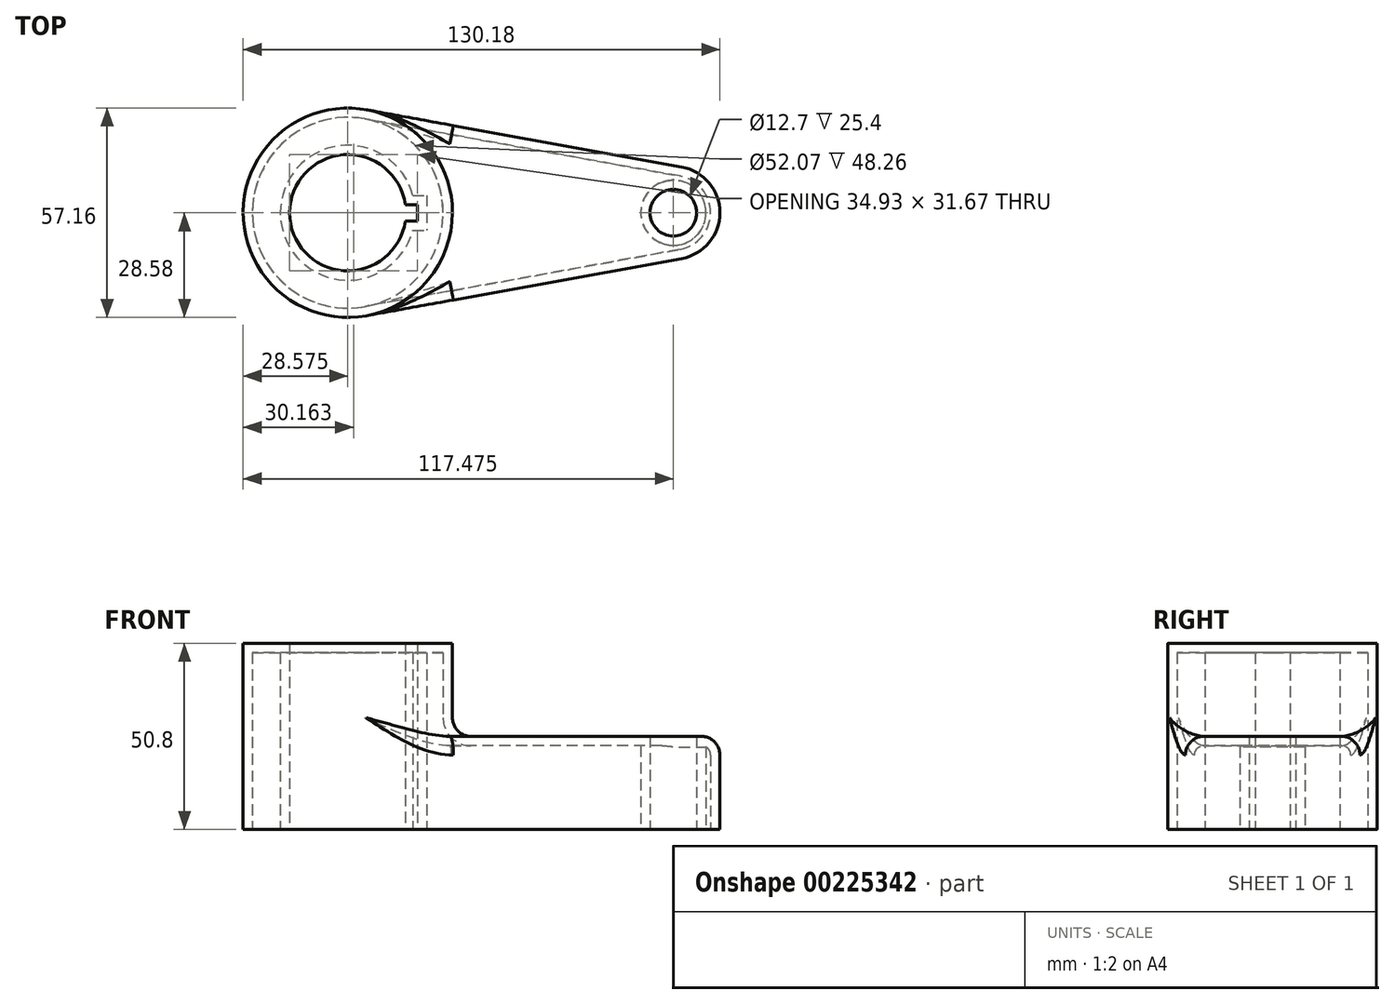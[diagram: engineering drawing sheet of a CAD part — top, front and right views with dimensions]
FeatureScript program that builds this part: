
annotation { "Feature Type Name" : "Feature", "Feature Type Description" : "" }
export const myFeature = defineFeature(function(context is Context, id is Id, definition is map)
    precondition{}
    {
        {
            var Q0;
            Q0=qCreatedBy(makeId("Top.planeOp"),FACE);
            var sketch = newSketch(context, id + "F0", { "sketchPlane" : qUnion([Q0])});
            skCircle(sketch, "E0", {"center": v(-65.9, 0) * mm, "radius": 28.58 * mm});
            skCircle(sketch, "E1", {"center": v(23, 0) * mm, "radius": 12.7 * mm});
            skLineSegment(sketch, "E2", {"start": v(-60.8, 28.12) * mm, "end": v(25.27, 12.5) * mm});
            skLineSegment(sketch, "E3", {"start": v(25.27, -12.5) * mm, "end": v(-60.8, -28.12) * mm});
            skCircle(sketch, "E4", {"center": v(-65.9, 0) * mm, "radius": 15.88 * mm});
            skCircle(sketch, "E5", {"center": v(23, 0) * mm, "radius": 6.35 * mm});
            skLineSegment(sketch, "E6.bottom", {"start": v(-50.18, 2.22) * mm, "end": v(-46.84, 2.22) * mm});
            skLineSegment(sketch, "E6.top", {"start": v(-50.18, -2.22) * mm, "end": v(-46.84, -2.22) * mm});
            skLineSegment(sketch, "E6.left", {"start": v(-50.18, 2.22) * mm, "end": v(-50.18, -2.22) * mm});
            skLineSegment(sketch, "E6.right", {"start": v(-46.84, 2.22) * mm, "end": v(-46.84, -2.22) * mm});
            skLineSegment(sketch, "E7", {"start": v(-65.9, 0) * mm, "end": v(-50.18, 2.22) * mm, "construction": true});
            skLineSegment(sketch, "E8", {"start": v(-65.9, 0) * mm, "end": v(-50.18, -2.22) * mm, "construction": true});
            skLineSegment(sketch, "E9", {"start": v(-65.9, 0) * mm, "end": v(-46.84, 0) * mm, "construction": true});
            skLineSegment(sketch, "E10", {"start": v(-81.77, 0) * mm, "end": v(-94.47, 0) * mm, "construction": true});
            skLineSegment(sketch, "E11", {"start": v(29.36, 0) * mm, "end": v(10.3, 0) * mm, "construction": true});
            skLineSegment(sketch, "E12", {"start": v(-65.9, 0) * mm, "end": v(23, 0) * mm, "construction": true});
            skSolve(sketch);
        }
        {
            var Q0;
            {var subQ0=sQuery(id+"F0.wireOp",EDGE,"E6.bottom");Q0=makeQuery(id+"F0.imprint","IMPRINT",FACE,{"disambiguationData":[TD([[makeQuery(id+"F0.imprint","IMPRINT",EDGE,{"derivedFrom":subQ0}),1.0]])]});}
            extrude(context, id + "F1", {"entities" : qUnion([Q0]), "depth" : 50.8 * mm});
        }
        {
            var Q0;
            Q0 = qSketchRegion(id + "F0", true);
            extrude(context, id + "F2", {"entities" : qUnion([Q0]), "operationType" : NewBodyOperationType.ADD, "depth" : 25.4 * mm});
        }
        {
            var Q0;
            {var subQ0=sQuery(id+"F0.wireOp",EDGE,"E0");Q0=makeQuery(id+"F2.boolean.opBoolean","INTERSECT",EDGE,{"derivedFrom":[makeQuery(id+"F1.opExtrude","SWEPT_FACE",FACE,{"disambiguationData":[OSD([subQ0])]}),makeQuery(id+"F2.opExtrude","CAP_FACE",FACE,{"disambiguationData":[OSD([subQ0,sQuery(id+"F0.wireOp",EDGE,"E1"),sQuery(id+"F0.wireOp",EDGE,"E2"),sQuery(id+"F0.wireOp",EDGE,"E3"),sQuery(id+"F0.wireOp",EDGE,"E4"),sQuery(id+"F0.wireOp",EDGE,"E5"),sQuery(id+"F0.wireOp",EDGE,"E6.bottom"),sQuery(id+"F0.wireOp",EDGE,"E6.top"),sQuery(id+"F0.wireOp",EDGE,"E6.right")])],"isStart":false})]});}
            fillet(context, id + "F3", {"entities" : qUnion([Q0]), "radius" : 5.08 * mm, "tangentPropagation" : true, "allowEdgeOverflow" : false});
        }
        {
            var Q0;
            Q0=makeQuery(id+"F2.opExtrude","CAP_EDGE",EDGE,{"disambiguationData":[OSD([sQuery(id+"F0.wireOp",EDGE,"E3")])],"isStart":false});
            fillet(context, id + "F4", {"entities" : qUnion([Q0]), "radius" : 5.08 * mm, "tangentPropagation" : true, "allowEdgeOverflow" : false});
        }
        {
            var Q0;
            {var subQ0=sQuery(id+"F0.wireOp",EDGE,"E6.right");var subQ1=sQuery(id+"F0.wireOp",EDGE,"E6.top");var subQ2=sQuery(id+"F0.wireOp",EDGE,"E6.bottom");var subQ3=sQuery(id+"F0.wireOp",EDGE,"E4");var subQ4=sQuery(id+"F0.wireOp",EDGE,"E0");Q0=makeQuery(id+"F2.boolean.opBoolean","MERGE",FACE,{"derivedFrom":[makeQuery(id+"F1.opExtrude","CAP_FACE",FACE,{"disambiguationData":[OSD([subQ4,subQ3,subQ2,subQ1,subQ0])],"isStart":true}),makeQuery(id+"F2.opExtrude","CAP_FACE",FACE,{"disambiguationData":[OSD([subQ4,sQuery(id+"F0.wireOp",EDGE,"E1"),sQuery(id+"F0.wireOp",EDGE,"E2"),sQuery(id+"F0.wireOp",EDGE,"E3"),subQ3,sQuery(id+"F0.wireOp",EDGE,"E5"),subQ2,subQ1,subQ0])],"isStart":true})]});}
            shell(context, id + "F5", {"entities" : qUnion([Q0]), "thickness" : 2.54 * mm});
        }
    });
